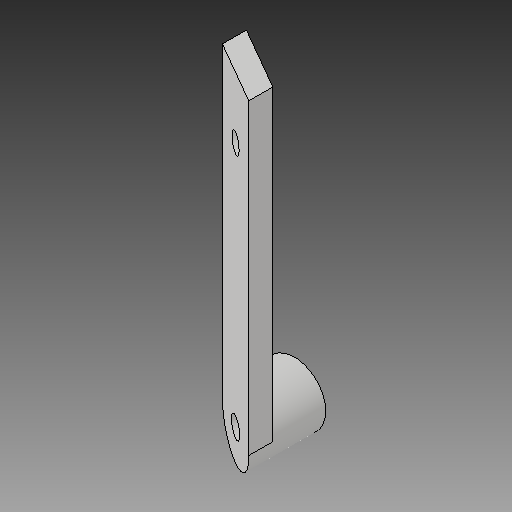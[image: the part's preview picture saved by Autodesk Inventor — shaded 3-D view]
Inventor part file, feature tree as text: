
AUTODESK INVENTOR PART (.ipt)
format: ipt  version: 2018 (Build 220112000, 112)  size: 153,600 bytes
history: native  units: mm
features: extrude x8, sketch x8, projected_geometry x6, fillet x1
ambient origin geometry x8: Origin, YZ Plane, XZ Plane, XY Plane, X Axis, Y Axis, Z Axis, Center Point
bodies: Solid1 (feature_tree)
feature tree (23):
  extrude  "Extrusion1"  Depth=5.0mm
  fillet  "Fillet1"  Radius=25.4mm
  extrude  "Extrusion2"  TaperAngle=0.0deg  [1 undecoded]
  extrude  "Extrusion3"  Depth=13.0mm
  extrude  "Extrusion4"  Depth=13.0mm
  extrude  "Extrusion5"  Depth=6.5mm
  extrude  "Extrusion6"  Depth=16.0mm TaperAngle=0.0deg
  extrude  "Extrusion7"  Depth=16.0mm TaperAngle=0.0deg
  extrude  "Extrusion8"  Depth=12.7mm
  sketch  "Sketch1"  dims[d1=150.0deg d2=5.0mm d5=25.4mm]
  sketch  "Sketch2"  dims[d6=0.0mm d7=0.0mm]
  sketch  "Sketch3"  dims[d8=14.664697mm d9=13.0mm]
  sketch  "Sketch4"  dims[d10=13.0mm d11=5.0mm]
  sketch  "Sketch5"  dims[d12=70.4mm d13=0.0mm d14=6.5mm]
  sketch  "Sketch6"  dims[d15=16.0mm d16=0.0mm d17=16.0mm d18=0.0mm]
  sketch  "Sketch7"  dims[d19=150.0deg d20=16.0mm d21=0.0mm]
  sketch  "Sketch9"  dims[d22=4.0mm d23=12.7mm d24=16.0mm d25=0.0mm d26=4.0mm d27=12.7mm d28=16.0mm d29=0.0mm d30=4.0mm d31=16.0mm d32=0.0mm d33=16.0mm d34=0.0mm]
  projected_geometry  "Project Cut Edges1"
  projected_geometry  "Project Cut Edges2"
  projected_geometry  "Project Cut Edges3"
  projected_geometry  "Project Cut Edges4"
  projected_geometry  "Project Cut Edges5"
  projected_geometry  "Project Cut Edges6"
note: 1 required parameter value undecoded (feature->parameter linkage not recoverable at this tier; creation-order binding heuristic only, values carry confidence <= 0.55)
